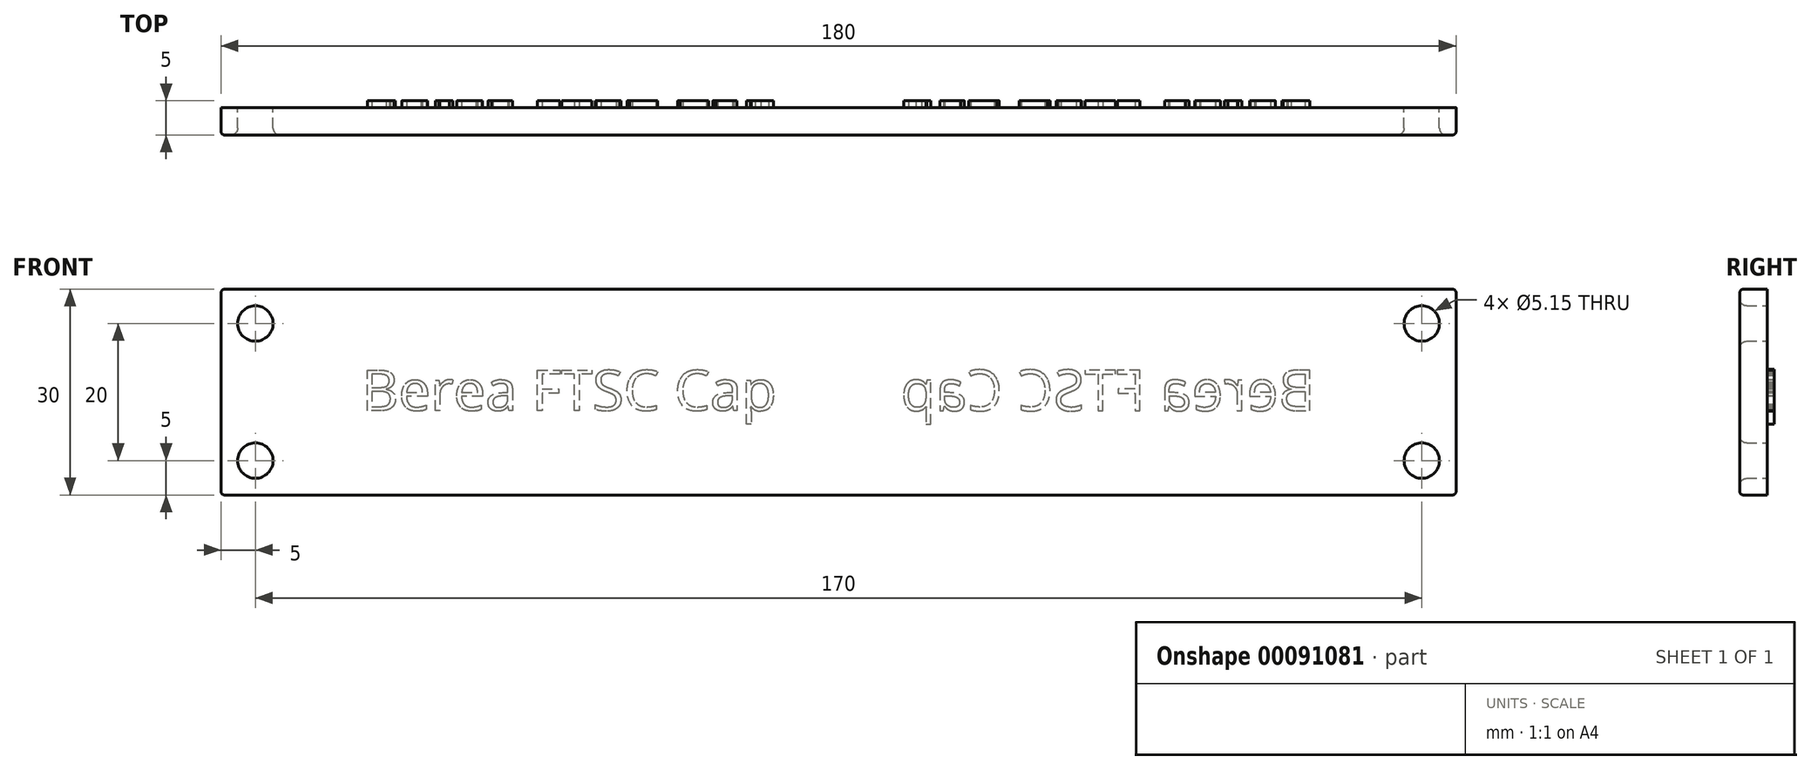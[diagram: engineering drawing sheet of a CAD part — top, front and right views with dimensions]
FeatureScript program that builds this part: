
annotation { "Feature Type Name" : "Feature", "Feature Type Description" : "" }
export const myFeature = defineFeature(function(context is Context, id is Id, definition is map)
    precondition{}
    {
        {
            var Q0;
            Q0=qCreatedBy(makeId("Front.planeOp"),FACE);
            var sketch = newSketch(context, id + "F0", { "sketchPlane" : qUnion([Q0])});
            skLineSegment(sketch, "E0.bottom", {"start": v(-90, -15) * mm, "end": v(90, -15) * mm});
            skLineSegment(sketch, "E0.top", {"start": v(-90, 15) * mm, "end": v(90, 15) * mm});
            skLineSegment(sketch, "E0.left", {"start": v(-90, -15) * mm, "end": v(-90, 15) * mm});
            skLineSegment(sketch, "E0.right", {"start": v(90, -15) * mm, "end": v(90, 15) * mm});
            skPoint(sketch, "E0.middle", {"position": v(0, 0) * mm});
            skCircle(sketch, "E1", {"center": v(-85, 10) * mm, "radius": 2.58 * mm});
            skPoint(sketch, "E2.start.orphan", {"position": v(-90, 0) * mm});
            skPoint(sketch, "E3.orphan", {"position": v(0, 15) * mm});
            skPoint(sketch, "E4.end.orphan", {"position": v(0, -15) * mm});
            skLineSegment(sketch, "E5", {"start": v(-90, 0) * mm, "end": v(0, 0) * mm, "construction": true});
            skLineSegment(sketch, "E6", {"start": v(0, 15) * mm, "end": v(0, -15) * mm, "construction": true});
            skCircle(sketch, "E7.MirrorC", {"center": v(-85, -10) * mm, "radius": 2.58 * mm});
            skCircle(sketch, "E8.MirrorC", {"center": v(85, 10) * mm, "radius": 2.58 * mm});
            skCircle(sketch, "E9.MirrorC", {"center": v(85, -10) * mm, "radius": 2.58 * mm});
            skSolve(sketch);
        }
        {
            var Q0;
            Q0=makeQuery(id+"F0.imprint","IMPRINT",FACE,{"disambiguationData":[TD([[makeQuery(id+"F0.imprint","IMPRINT",EDGE,{"derivedFrom":sQuery(id+"F0.wireOp",EDGE,"E0.bottom")}),1.0]])]});
            extrude(context, id + "F1", {"entities" : qUnion([Q0]), "depth" : 4 * mm});
        }
        {
            var Q0;
            Q0=makeQuery(id+"F1.opExtrude","CAP_EDGE",EDGE,{"disambiguationData":[OSD([sQuery(id+"F0.wireOp",EDGE,"E1")])],"isStart":false});
            var Q1;
            Q1=makeQuery(id+"F1.opExtrude","CAP_EDGE",EDGE,{"disambiguationData":[OSD([sQuery(id+"F0.wireOp",EDGE,"f5b72a5b-8583-449a-bdbf-9ac5a681e1fd0.MirrorC")])],"isStart":false});
            var Q2;
            Q2=makeQuery(id+"F1.opExtrude","CAP_EDGE",EDGE,{"disambiguationData":[OSD([sQuery(id+"F0.wireOp",EDGE,"2623e306-60f4-4522-aa65-1e3e8c2cf5b60.MirrorC")])],"isStart":false});
            var Q3;
            Q3=makeQuery(id+"F1.opExtrude","CAP_EDGE",EDGE,{"disambiguationData":[OSD([sQuery(id+"F0.wireOp",EDGE,"be81a34d-1d50-4ce7-a7a8-4484a1701fac0.MirrorC")])],"isStart":false});
            var Q4;
            Q4=makeQuery(id+"F1.opExtrude","CAP_EDGE",EDGE,{"disambiguationData":[OSD([sQuery(id+"F0.wireOp",EDGE,"E7.MirrorC")])],"isStart":false});
            var Q5;
            Q5=makeQuery(id+"F1.opExtrude","CAP_EDGE",EDGE,{"disambiguationData":[OSD([sQuery(id+"F0.wireOp",EDGE,"E8.MirrorC")])],"isStart":false});
            var Q6;
            Q6=makeQuery(id+"F1.opExtrude","CAP_EDGE",EDGE,{"disambiguationData":[OSD([sQuery(id+"F0.wireOp",EDGE,"E9.MirrorC")])],"isStart":false});
            fillet(context, id + "F2", {"entities" : qUnion([Q0, Q1, Q2, Q3, Q4, Q5, Q6]), "radius" : 1 * mm, "tangentPropagation" : true, "allowEdgeOverflow" : false});
        }
        {
            var Q0;
            Q0=makeQuery(id+"F1.opExtrude","CAP_EDGE",EDGE,{"disambiguationData":[OSD([sQuery(id+"F0.wireOp",EDGE,"E0.top")])],"isStart":false});
            var Q1;
            Q1=makeQuery(id+"F1.opExtrude","CAP_EDGE",EDGE,{"disambiguationData":[OSD([sQuery(id+"F0.wireOp",EDGE,"E0.left")])],"isStart":false});
            var Q2;
            Q2=makeQuery(id+"F1.opExtrude","CAP_EDGE",EDGE,{"disambiguationData":[OSD([sQuery(id+"F0.wireOp",EDGE,"E0.bottom")])],"isStart":false});
            var Q3;
            Q3=makeQuery(id+"F1.opExtrude","CAP_EDGE",EDGE,{"disambiguationData":[OSD([sQuery(id+"F0.wireOp",EDGE,"E0.right")])],"isStart":false});
            var Q4;
            Q4=makeQuery(id+"F1.opExtrude","SWEPT_EDGE",EDGE,{"disambiguationData":[OSD([sQuery(id+"F0.wireOp",EDGE,"E0.top"),sQuery(id+"F0.wireOp",EDGE,"E0.left")])]});
            var Q5;
            Q5=makeQuery(id+"F1.opExtrude","SWEPT_EDGE",EDGE,{"disambiguationData":[OSD([sQuery(id+"F0.wireOp",EDGE,"E0.bottom"),sQuery(id+"F0.wireOp",EDGE,"E0.left")])]});
            var Q6;
            Q6=makeQuery(id+"F1.opExtrude","SWEPT_EDGE",EDGE,{"disambiguationData":[OSD([sQuery(id+"F0.wireOp",EDGE,"E0.top"),sQuery(id+"F0.wireOp",EDGE,"E0.right")])]});
            var Q7;
            Q7=makeQuery(id+"F1.opExtrude","SWEPT_EDGE",EDGE,{"disambiguationData":[OSD([sQuery(id+"F0.wireOp",EDGE,"E0.bottom"),sQuery(id+"F0.wireOp",EDGE,"E0.right")])]});
            fillet(context, id + "F3", {"entities" : qUnion([Q0, Q1, Q2, Q3, Q4, Q5, Q6, Q7]), "radius" : .5 * mm, "tangentPropagation" : true, "allowEdgeOverflow" : false});
        }
        {
            var Q0;
            Q0=makeQuery(id+"F1.opExtrude","CAP_FACE",FACE,{"disambiguationData":[OSD([sQuery(id+"F0.wireOp",EDGE,"E0.bottom"),sQuery(id+"F0.wireOp",EDGE,"E0.top"),sQuery(id+"F0.wireOp",EDGE,"E0.left"),sQuery(id+"F0.wireOp",EDGE,"E0.right"),sQuery(id+"F0.wireOp",EDGE,"E1"),sQuery(id+"F0.wireOp",EDGE,"E7.MirrorC"),sQuery(id+"F0.wireOp",EDGE,"E8.MirrorC"),sQuery(id+"F0.wireOp",EDGE,"E9.MirrorC")])],"isStart":true});
            var sketch = newSketch(context, id + "F4", { "sketchPlane" : qUnion([Q0])});
            skText(sketch, "E10", { "text": "Berea FTSC Cap", "fontName": "OpenSans-Regular.ttf"});
            skLineSegment(sketch, "E11", {"start": v(0, 15) * mm, "end": v(0, -15) * mm, "construction": true});
            const initialGuessF4  = {"E10": [-0.0695, -0.0027, 1, 0, 0.00596]};
            skSetInitialGuess(sketch, initialGuessF4);
            skSolve(sketch);
        }
        {
            var Q0;
            Q0=qSketchRegion(id+"F4",true);
            extrude(context, id + "F5", {"entities" : qUnion([Q0]), "operationType" : NewBodyOperationType.ADD, "depth" : 1 * mm});
        }
        {
            var Q0;
            Q0=makeQuery(id+"F1.opExtrude","SWEPT_BODY",BODY,{"disambiguationData":[OSD([sQuery(id+"F0.wireOp",EDGE,"E0.bottom"),sQuery(id+"F0.wireOp",EDGE,"E0.top"),sQuery(id+"F0.wireOp",EDGE,"E0.left"),sQuery(id+"F0.wireOp",EDGE,"E0.right"),sQuery(id+"F0.wireOp",EDGE,"E1"),sQuery(id+"F0.wireOp",EDGE,"E7.MirrorC"),sQuery(id+"F0.wireOp",EDGE,"E8.MirrorC"),sQuery(id+"F0.wireOp",EDGE,"E9.MirrorC")])]});
            var Q1;
            Q1=makeQuery(id+"F5.opExtrude","SWEPT_FACE",FACE,{"disambiguationData":[OSD([sQuery(id+"F4.wireOp",EDGE,"E10.sketch_text.stroke-94")])]});
            var Q2;
            Q2=makeQuery(id+"F5.opExtrude","SWEPT_FACE",FACE,{"disambiguationData":[OSD([sQuery(id+"F4.wireOp",EDGE,"E10.sketch_text.stroke-169")])]});
            var Q3;
            Q3=makeQuery(id+"F5.opExtrude","SWEPT_FACE",FACE,{"disambiguationData":[OSD([sQuery(id+"F4.wireOp",EDGE,"E10.sketch_text.stroke-185")])]});
            var Q4;
            Q4=makeQuery(id+"F5.opExtrude","SWEPT_FACE",FACE,{"disambiguationData":[OSD([sQuery(id+"F4.wireOp",EDGE,"E10.sketch_text.stroke-125")])]});
            var Q5;
            Q5=makeQuery(id+"F5.opExtrude","SWEPT_FACE",FACE,{"disambiguationData":[OSD([sQuery(id+"F4.wireOp",EDGE,"E10.sketch_text.stroke-155")])]});
            var Q6;
            Q6=makeQuery(id+"F5.opExtrude","SWEPT_FACE",FACE,{"disambiguationData":[OSD([sQuery(id+"F4.wireOp",EDGE,"E10.sketch_text.stroke-65")])]});
            var Q7;
            Q7=makeQuery(id+"F5.opExtrude","SWEPT_FACE",FACE,{"disambiguationData":[OSD([sQuery(id+"F4.wireOp",EDGE,"E10.sketch_text.stroke-81")])]});
            var Q8;
            Q8=makeQuery(id+"F5.opExtrude","SWEPT_FACE",FACE,{"disambiguationData":[OSD([sQuery(id+"F4.wireOp",EDGE,"E10.sketch_text.stroke-67")])]});
            var Q9;
            Q9=makeQuery(id+"F5.opExtrude","SWEPT_FACE",FACE,{"disambiguationData":[OSD([sQuery(id+"F4.wireOp",EDGE,"E10.sketch_text.stroke-99")])]});
            var Q10;
            Q10=makeQuery(id+"F5.opExtrude","SWEPT_FACE",FACE,{"disambiguationData":[OSD([sQuery(id+"F4.wireOp",EDGE,"E10.sketch_text.stroke-127")])]});
            var Q11;
            Q11=makeQuery(id+"F5.opExtrude","SWEPT_FACE",FACE,{"disambiguationData":[OSD([sQuery(id+"F4.wireOp",EDGE,"E10.sketch_text.stroke-10")])]});
            var Q12;
            Q12=makeQuery(id+"F5.opExtrude","CAP_FACE",FACE,{"disambiguationData":[OSD([sQuery(id+"F4.wireOp",EDGE,"E10.sketch_text.stroke-9"),sQuery(id+"F4.wireOp",EDGE,"E10.sketch_text.stroke-10"),sQuery(id+"F4.wireOp",EDGE,"E10.sketch_text.stroke-11"),sQuery(id+"F4.wireOp",EDGE,"E10.sketch_text.stroke-12")])],"isStart":false});
            var Q13;
            Q13=makeQuery(id+"F5.opExtrude","SWEPT_FACE",FACE,{"disambiguationData":[OSD([sQuery(id+"F4.wireOp",EDGE,"E10.sketch_text.stroke-154")])]});
            var Q14;
            Q14=makeQuery(id+"F5.opExtrude","SWEPT_FACE",FACE,{"disambiguationData":[OSD([sQuery(id+"F4.wireOp",EDGE,"E10.sketch_text.stroke-1")])]});
            var Q15;
            Q15=makeQuery(id+"F5.opExtrude","CAP_FACE",FACE,{"disambiguationData":[OSD([sQuery(id+"F4.wireOp",EDGE,"E10.sketch_text.stroke-124"),sQuery(id+"F4.wireOp",EDGE,"E10.sketch_text.stroke-125"),sQuery(id+"F4.wireOp",EDGE,"E10.sketch_text.stroke-126"),sQuery(id+"F4.wireOp",EDGE,"E10.sketch_text.stroke-127"),sQuery(id+"F4.wireOp",EDGE,"E10.sketch_text.stroke-128"),sQuery(id+"F4.wireOp",EDGE,"E10.sketch_text.stroke-129"),sQuery(id+"F4.wireOp",EDGE,"E10.sketch_text.stroke-130"),sQuery(id+"F4.wireOp",EDGE,"E10.sketch_text.stroke-131"),sQuery(id+"F4.wireOp",EDGE,"E10.sketch_text.stroke-132"),sQuery(id+"F4.wireOp",EDGE,"E10.sketch_text.stroke-133"),sQuery(id+"F4.wireOp",EDGE,"E10.sketch_text.stroke-134"),sQuery(id+"F4.wireOp",EDGE,"E10.sketch_text.stroke-135"),sQuery(id+"F4.wireOp",EDGE,"E10.sketch_text.stroke-136"),sQuery(id+"F4.wireOp",EDGE,"E10.sketch_text.stroke-137"),sQuery(id+"F4.wireOp",EDGE,"E10.sketch_text.stroke-138")])],"isStart":false});
            var Q16;
            Q16=makeQuery(id+"F5.opExtrude","CAP_FACE",FACE,{"disambiguationData":[OSD([sQuery(id+"F4.wireOp",EDGE,"E10.sketch_text.stroke-34"),sQuery(id+"F4.wireOp",EDGE,"E10.sketch_text.stroke-35"),sQuery(id+"F4.wireOp",EDGE,"E10.sketch_text.stroke-36"),sQuery(id+"F4.wireOp",EDGE,"E10.sketch_text.stroke-37"),sQuery(id+"F4.wireOp",EDGE,"E10.sketch_text.stroke-38"),sQuery(id+"F4.wireOp",EDGE,"E10.sketch_text.stroke-39"),sQuery(id+"F4.wireOp",EDGE,"E10.sketch_text.stroke-40"),sQuery(id+"F4.wireOp",EDGE,"E10.sketch_text.stroke-41"),sQuery(id+"F4.wireOp",EDGE,"E10.sketch_text.stroke-42"),sQuery(id+"F4.wireOp",EDGE,"E10.sketch_text.stroke-43"),sQuery(id+"F4.wireOp",EDGE,"E10.sketch_text.stroke-44"),sQuery(id+"F4.wireOp",EDGE,"E10.sketch_text.stroke-45"),sQuery(id+"F4.wireOp",EDGE,"E10.sketch_text.stroke-46"),sQuery(id+"F4.wireOp",EDGE,"E10.sketch_text.stroke-47"),sQuery(id+"F4.wireOp",EDGE,"E10.sketch_text.stroke-48"),sQuery(id+"F4.wireOp",EDGE,"E10.sketch_text.stroke-49"),sQuery(id+"F4.wireOp",EDGE,"E10.sketch_text.stroke-50"),sQuery(id+"F4.wireOp",EDGE,"E10.sketch_text.stroke-51"),sQuery(id+"F4.wireOp",EDGE,"E10.sketch_text.stroke-52"),sQuery(id+"F4.wireOp",EDGE,"E10.sketch_text.stroke-53"),sQuery(id+"F4.wireOp",EDGE,"E10.sketch_text.stroke-54"),sQuery(id+"F4.wireOp",EDGE,"E10.sketch_text.stroke-55"),sQuery(id+"F4.wireOp",EDGE,"E10.sketch_text.stroke-56"),sQuery(id+"F4.wireOp",EDGE,"E10.sketch_text.stroke-57"),sQuery(id+"F4.wireOp",EDGE,"E10.sketch_text.stroke-58"),sQuery(id+"F4.wireOp",EDGE,"E10.sketch_text.stroke-59"),sQuery(id+"F4.wireOp",EDGE,"E10.sketch_text.stroke-60")])],"isStart":false});
            var Q17;
            Q17=makeQuery(id+"F5.opExtrude","SWEPT_FACE",FACE,{"disambiguationData":[OSD([sQuery(id+"F4.wireOp",EDGE,"E10.sketch_text.stroke-50")])]});
            var Q18;
            Q18=makeQuery(id+"F5.opExtrude","SWEPT_FACE",FACE,{"disambiguationData":[OSD([sQuery(id+"F4.wireOp",EDGE,"E10.sketch_text.stroke-2")])]});
            var Q19;
            Q19=makeQuery(id+"F5.opExtrude","SWEPT_FACE",FACE,{"disambiguationData":[OSD([sQuery(id+"F4.wireOp",EDGE,"E10.sketch_text.stroke-3")])]});
            var Q20;
            Q20=makeQuery(id+"F5.opExtrude","SWEPT_FACE",FACE,{"disambiguationData":[OSD([sQuery(id+"F4.wireOp",EDGE,"E10.sketch_text.stroke-5")])]});
            var Q21;
            Q21=makeQuery(id+"F5.opExtrude","SWEPT_FACE",FACE,{"disambiguationData":[OSD([sQuery(id+"F4.wireOp",EDGE,"E10.sketch_text.stroke-8")])]});
            var Q22;
            Q22=makeQuery(id+"F5.opExtrude","SWEPT_FACE",FACE,{"disambiguationData":[OSD([sQuery(id+"F4.wireOp",EDGE,"E10.sketch_text.stroke-98")])]});
            var Q23;
            Q23=makeQuery(id+"F5.opExtrude","SWEPT_FACE",FACE,{"disambiguationData":[OSD([sQuery(id+"F4.wireOp",EDGE,"E10.sketch_text.stroke-66")])]});
            var Q24;
            Q24=makeQuery(id+"F5.opExtrude","SWEPT_FACE",FACE,{"disambiguationData":[OSD([sQuery(id+"F4.wireOp",EDGE,"E10.sketch_text.stroke-153")])]});
            var Q25;
            Q25=makeQuery(id+"F5.opExtrude","SWEPT_FACE",FACE,{"disambiguationData":[OSD([sQuery(id+"F4.wireOp",EDGE,"E10.sketch_text.stroke-126")])]});
            var Q26;
            Q26=makeQuery(id+"F5.opExtrude","SWEPT_FACE",FACE,{"disambiguationData":[OSD([sQuery(id+"F4.wireOp",EDGE,"E10.sketch_text.stroke-183")])]});
            var Q27;
            Q27=makeQuery(id+"F5.opExtrude","SWEPT_FACE",FACE,{"disambiguationData":[OSD([sQuery(id+"F4.wireOp",EDGE,"E10.sketch_text.stroke-109")])]});
            var Q28;
            Q28=makeQuery(id+"F5.opExtrude","SWEPT_FACE",FACE,{"disambiguationData":[OSD([sQuery(id+"F4.wireOp",EDGE,"E10.sketch_text.stroke-186")])]});
            var Q29;
            Q29=makeQuery(id+"F5.opExtrude","SWEPT_FACE",FACE,{"disambiguationData":[OSD([sQuery(id+"F4.wireOp",EDGE,"E10.sketch_text.stroke-79")])]});
            var Q30;
            Q30=makeQuery(id+"F5.opExtrude","SWEPT_FACE",FACE,{"disambiguationData":[OSD([sQuery(id+"F4.wireOp",EDGE,"E10.sketch_text.stroke-110")])]});
            var Q31;
            Q31=makeQuery(id+"F5.opExtrude","SWEPT_FACE",FACE,{"disambiguationData":[OSD([sQuery(id+"F4.wireOp",EDGE,"E10.sketch_text.stroke-38")])]});
            var Q32;
            Q32=makeQuery(id+"F5.opExtrude","SWEPT_FACE",FACE,{"disambiguationData":[OSD([sQuery(id+"F4.wireOp",EDGE,"E10.sketch_text.stroke-24")])]});
            var Q33;
            Q33=makeQuery(id+"F5.opExtrude","SWEPT_FACE",FACE,{"disambiguationData":[OSD([sQuery(id+"F4.wireOp",EDGE,"E10.sketch_text.stroke-12")])]});
            var Q34;
            Q34=makeQuery(id+"F5.opExtrude","SWEPT_FACE",FACE,{"disambiguationData":[OSD([sQuery(id+"F4.wireOp",EDGE,"E10.sketch_text.stroke-100")])]});
            var Q35;
            Q35=makeQuery(id+"F5.opExtrude","SWEPT_FACE",FACE,{"disambiguationData":[OSD([sQuery(id+"F4.wireOp",EDGE,"E10.sketch_text.stroke-158")])]});
            var Q36;
            Q36=makeQuery(id+"F5.opExtrude","SWEPT_FACE",FACE,{"disambiguationData":[OSD([sQuery(id+"F4.wireOp",EDGE,"E10.sketch_text.stroke-142")])]});
            var Q37;
            Q37=makeQuery(id+"F5.opExtrude","SWEPT_FACE",FACE,{"disambiguationData":[OSD([sQuery(id+"F4.wireOp",EDGE,"E10.sketch_text.stroke-54")])]});
            var Q38;
            Q38=makeQuery(id+"F5.opExtrude","SWEPT_FACE",FACE,{"disambiguationData":[OSD([sQuery(id+"F4.wireOp",EDGE,"E10.sketch_text.stroke-25")])]});
            var Q39;
            Q39=makeQuery(id+"F5.opExtrude","SWEPT_FACE",FACE,{"disambiguationData":[OSD([sQuery(id+"F4.wireOp",EDGE,"E10.sketch_text.stroke-101")])]});
            var Q40;
            Q40=makeQuery(id+"F5.opExtrude","SWEPT_FACE",FACE,{"disambiguationData":[OSD([sQuery(id+"F4.wireOp",EDGE,"E10.sketch_text.stroke-69")])]});
            var Q41;
            Q41=makeQuery(id+"F5.opExtrude","SWEPT_FACE",FACE,{"disambiguationData":[OSD([sQuery(id+"F4.wireOp",EDGE,"E10.sketch_text.stroke-159")])]});
            var Q42;
            Q42=makeQuery(id+"F5.opExtrude","SWEPT_FACE",FACE,{"disambiguationData":[OSD([sQuery(id+"F4.wireOp",EDGE,"E10.sketch_text.stroke-85")])]});
            var Q43;
            Q43=makeQuery(id+"F5.opExtrude","SWEPT_FACE",FACE,{"disambiguationData":[OSD([sQuery(id+"F4.wireOp",EDGE,"E10.sketch_text.stroke-173")])]});
            var Q44;
            Q44=makeQuery(id+"F5.opExtrude","SWEPT_FACE",FACE,{"disambiguationData":[OSD([sQuery(id+"F4.wireOp",EDGE,"E10.sketch_text.stroke-40")])]});
            var Q45;
            Q45=makeQuery(id+"F5.opExtrude","SWEPT_FACE",FACE,{"disambiguationData":[OSD([sQuery(id+"F4.wireOp",EDGE,"E10.sketch_text.stroke-102")])]});
            var Q46;
            Q46=makeQuery(id+"F5.opExtrude","SWEPT_FACE",FACE,{"disambiguationData":[OSD([sQuery(id+"F4.wireOp",EDGE,"E10.sketch_text.stroke-86")])]});
            var Q47;
            Q47=makeQuery(id+"F5.opExtrude","SWEPT_FACE",FACE,{"disambiguationData":[OSD([sQuery(id+"F4.wireOp",EDGE,"E10.sketch_text.stroke-130")])]});
            var Q48;
            Q48=makeQuery(id+"F5.opExtrude","SWEPT_FACE",FACE,{"disambiguationData":[OSD([sQuery(id+"F4.wireOp",EDGE,"E10.sketch_text.stroke-103")])]});
            var Q49;
            Q49=makeQuery(id+"F5.opExtrude","SWEPT_FACE",FACE,{"disambiguationData":[OSD([sQuery(id+"F4.wireOp",EDGE,"E10.sketch_text.stroke-87")])]});
            var Q50;
            Q50=makeQuery(id+"F5.opExtrude","SWEPT_FACE",FACE,{"disambiguationData":[OSD([sQuery(id+"F4.wireOp",EDGE,"E10.sketch_text.stroke-145")])]});
            var Q51;
            Q51=makeQuery(id+"F5.opExtrude","SWEPT_FACE",FACE,{"disambiguationData":[OSD([sQuery(id+"F4.wireOp",EDGE,"E10.sketch_text.stroke-131")])]});
            var Q52;
            Q52=makeQuery(id+"F5.opExtrude","SWEPT_FACE",FACE,{"disambiguationData":[OSD([sQuery(id+"F4.wireOp",EDGE,"E10.sketch_text.stroke-28")])]});
            var Q53;
            Q53=makeQuery(id+"F5.opExtrude","SWEPT_FACE",FACE,{"disambiguationData":[OSD([sQuery(id+"F4.wireOp",EDGE,"E10.sketch_text.stroke-14")])]});
            var Q54;
            Q54=makeQuery(id+"F5.opExtrude","SWEPT_FACE",FACE,{"disambiguationData":[OSD([sQuery(id+"F4.wireOp",EDGE,"E10.sketch_text.stroke-88")])]});
            var Q55;
            Q55=makeQuery(id+"F5.opExtrude","SWEPT_FACE",FACE,{"disambiguationData":[OSD([sQuery(id+"F4.wireOp",EDGE,"E10.sketch_text.stroke-162")])]});
            var Q56;
            Q56=makeQuery(id+"F5.opExtrude","SWEPT_FACE",FACE,{"disambiguationData":[OSD([sQuery(id+"F4.wireOp",EDGE,"E10.sketch_text.stroke-176")])]});
            var Q57;
            Q57=makeQuery(id+"F5.opExtrude","SWEPT_FACE",FACE,{"disambiguationData":[OSD([sQuery(id+"F4.wireOp",EDGE,"E10.sketch_text.stroke-73")])]});
            var Q58;
            Q58=makeQuery(id+"F5.opExtrude","SWEPT_FACE",FACE,{"disambiguationData":[OSD([sQuery(id+"F4.wireOp",EDGE,"E10.sketch_text.stroke-59")])]});
            var Q59;
            Q59=makeQuery(id+"F5.opExtrude","SWEPT_FACE",FACE,{"disambiguationData":[OSD([sQuery(id+"F4.wireOp",EDGE,"E10.sketch_text.stroke-133")])]});
            var Q60;
            Q60=makeQuery(id+"F5.opExtrude","SWEPT_FACE",FACE,{"disambiguationData":[OSD([sQuery(id+"F4.wireOp",EDGE,"E10.sketch_text.stroke-119")])]});
            var Q61;
            Q61=makeQuery(id+"F5.opExtrude","SWEPT_FACE",FACE,{"disambiguationData":[OSD([sQuery(id+"F4.wireOp",EDGE,"E10.sketch_text.stroke-74")])]});
            var Q62;
            Q62=makeQuery(id+"F5.opExtrude","SWEPT_FACE",FACE,{"disambiguationData":[OSD([sQuery(id+"F4.wireOp",EDGE,"E10.sketch_text.stroke-44")])]});
            var Q63;
            Q63=makeQuery(id+"F5.opExtrude","SWEPT_FACE",FACE,{"disambiguationData":[OSD([sQuery(id+"F4.wireOp",EDGE,"E10.sketch_text.stroke-120")])]});
            var Q64;
            Q64=makeQuery(id+"F5.opExtrude","SWEPT_FACE",FACE,{"disambiguationData":[OSD([sQuery(id+"F4.wireOp",EDGE,"E10.sketch_text.stroke-90")])]});
            var Q65;
            Q65=makeQuery(id+"F5.opExtrude","SWEPT_FACE",FACE,{"disambiguationData":[OSD([sQuery(id+"F4.wireOp",EDGE,"E10.sketch_text.stroke-178")])]});
            var Q66;
            Q66=makeQuery(id+"F5.opExtrude","SWEPT_FACE",FACE,{"disambiguationData":[OSD([sQuery(id+"F4.wireOp",EDGE,"E10.sketch_text.stroke-45")])]});
            var Q67;
            Q67=makeQuery(id+"F5.opExtrude","SWEPT_FACE",FACE,{"disambiguationData":[OSD([sQuery(id+"F4.wireOp",EDGE,"E10.sketch_text.stroke-31")])]});
            var Q68;
            Q68=makeQuery(id+"F5.opExtrude","SWEPT_FACE",FACE,{"disambiguationData":[OSD([sQuery(id+"F4.wireOp",EDGE,"E10.sketch_text.stroke-135")])]});
            var Q69;
            Q69=makeQuery(id+"F5.opExtrude","SWEPT_FACE",FACE,{"disambiguationData":[OSD([sQuery(id+"F4.wireOp",EDGE,"E10.sketch_text.stroke-179")])]});
            var Q70;
            Q70=makeQuery(id+"F5.opExtrude","SWEPT_FACE",FACE,{"disambiguationData":[OSD([sQuery(id+"F4.wireOp",EDGE,"E10.sketch_text.stroke-165")])]});
            var Q71;
            Q71=makeQuery(id+"F5.opExtrude","SWEPT_FACE",FACE,{"disambiguationData":[OSD([sQuery(id+"F4.wireOp",EDGE,"E10.sketch_text.stroke-149")])]});
            var Q72;
            Q72=makeQuery(id+"F5.opExtrude","SWEPT_FACE",FACE,{"disambiguationData":[OSD([sQuery(id+"F4.wireOp",EDGE,"E10.sketch_text.stroke-136")])]});
            var Q73;
            Q73=makeQuery(id+"F5.opExtrude","SWEPT_FACE",FACE,{"disambiguationData":[OSD([sQuery(id+"F4.wireOp",EDGE,"E10.sketch_text.stroke-122")])]});
            var Q74;
            Q74=makeQuery(id+"F5.opExtrude","SWEPT_FACE",FACE,{"disambiguationData":[OSD([sQuery(id+"F4.wireOp",EDGE,"E10.sketch_text.stroke-106")])]});
            var Q75;
            Q75=makeQuery(id+"F5.opExtrude","SWEPT_FACE",FACE,{"disambiguationData":[OSD([sQuery(id+"F4.wireOp",EDGE,"E10.sketch_text.stroke-180")])]});
            var Q76;
            Q76=makeQuery(id+"F5.opExtrude","SWEPT_FACE",FACE,{"disambiguationData":[OSD([sQuery(id+"F4.wireOp",EDGE,"E10.sketch_text.stroke-166")])]});
            var Q77;
            Q77=makeQuery(id+"F5.opExtrude","SWEPT_FACE",FACE,{"disambiguationData":[OSD([sQuery(id+"F4.wireOp",EDGE,"E10.sketch_text.stroke-150")])]});
            var Q78;
            Q78=makeQuery(id+"F5.opExtrude","SWEPT_FACE",FACE,{"disambiguationData":[OSD([sQuery(id+"F4.wireOp",EDGE,"E10.sketch_text.stroke-76")])]});
            var Q79;
            Q79=makeQuery(id+"F5.opExtrude","SWEPT_FACE",FACE,{"disambiguationData":[OSD([sQuery(id+"F4.wireOp",EDGE,"E10.sketch_text.stroke-32")])]});
            var Q80;
            Q80=makeQuery(id+"F5.opExtrude","SWEPT_FACE",FACE,{"disambiguationData":[OSD([sQuery(id+"F4.wireOp",EDGE,"E10.sketch_text.stroke-181")])]});
            var Q81;
            Q81=makeQuery(id+"F5.opExtrude","SWEPT_FACE",FACE,{"disambiguationData":[OSD([sQuery(id+"F4.wireOp",EDGE,"E10.sketch_text.stroke-47")])]});
            var Q82;
            Q82=makeQuery(id+"F5.opExtrude","SWEPT_FACE",FACE,{"disambiguationData":[OSD([sQuery(id+"F4.wireOp",EDGE,"E10.sketch_text.stroke-123")])]});
            var Q83;
            Q83=makeQuery(id+"F5.opExtrude","SWEPT_FACE",FACE,{"disambiguationData":[OSD([sQuery(id+"F4.wireOp",EDGE,"E10.sketch_text.stroke-107")])]});
            var Q84;
            Q84=makeQuery(id+"F5.opExtrude","SWEPT_FACE",FACE,{"disambiguationData":[OSD([sQuery(id+"F4.wireOp",EDGE,"E10.sketch_text.stroke-48")])]});
            var Q85;
            Q85=makeQuery(id+"F5.opExtrude","SWEPT_FACE",FACE,{"disambiguationData":[OSD([sQuery(id+"F4.wireOp",EDGE,"E10.sketch_text.stroke-124")])]});
            var Q86;
            Q86=makeQuery(id+"F5.opExtrude","SWEPT_FACE",FACE,{"disambiguationData":[OSD([sQuery(id+"F4.wireOp",EDGE,"E10.sketch_text.stroke-108")])]});
            var Q87;
            Q87=makeQuery(id+"F5.opExtrude","CAP_FACE",FACE,{"disambiguationData":[OSD([sQuery(id+"F4.wireOp",EDGE,"E10.sketch_text.stroke-139"),sQuery(id+"F4.wireOp",EDGE,"E10.sketch_text.stroke-140"),sQuery(id+"F4.wireOp",EDGE,"E10.sketch_text.stroke-141"),sQuery(id+"F4.wireOp",EDGE,"E10.sketch_text.stroke-142"),sQuery(id+"F4.wireOp",EDGE,"E10.sketch_text.stroke-143"),sQuery(id+"F4.wireOp",EDGE,"E10.sketch_text.stroke-144"),sQuery(id+"F4.wireOp",EDGE,"E10.sketch_text.stroke-145"),sQuery(id+"F4.wireOp",EDGE,"E10.sketch_text.stroke-146"),sQuery(id+"F4.wireOp",EDGE,"E10.sketch_text.stroke-147"),sQuery(id+"F4.wireOp",EDGE,"E10.sketch_text.stroke-148"),sQuery(id+"F4.wireOp",EDGE,"E10.sketch_text.stroke-149"),sQuery(id+"F4.wireOp",EDGE,"E10.sketch_text.stroke-150"),sQuery(id+"F4.wireOp",EDGE,"E10.sketch_text.stroke-151"),sQuery(id+"F4.wireOp",EDGE,"E10.sketch_text.stroke-152"),sQuery(id+"F4.wireOp",EDGE,"E10.sketch_text.stroke-153"),sQuery(id+"F4.wireOp",EDGE,"E10.sketch_text.stroke-154"),sQuery(id+"F4.wireOp",EDGE,"E10.sketch_text.stroke-155"),sQuery(id+"F4.wireOp",EDGE,"E10.sketch_text.stroke-156"),sQuery(id+"F4.wireOp",EDGE,"E10.sketch_text.stroke-157"),sQuery(id+"F4.wireOp",EDGE,"E10.sketch_text.stroke-158"),sQuery(id+"F4.wireOp",EDGE,"E10.sketch_text.stroke-159"),sQuery(id+"F4.wireOp",EDGE,"E10.sketch_text.stroke-160"),sQuery(id+"F4.wireOp",EDGE,"E10.sketch_text.stroke-161"),sQuery(id+"F4.wireOp",EDGE,"E10.sketch_text.stroke-162"),sQuery(id+"F4.wireOp",EDGE,"E10.sketch_text.stroke-163"),sQuery(id+"F4.wireOp",EDGE,"E10.sketch_text.stroke-164"),sQuery(id+"F4.wireOp",EDGE,"E10.sketch_text.stroke-165")])],"isStart":false});
            var Q88;
            Q88=makeQuery(id+"F5.opExtrude","CAP_FACE",FACE,{"disambiguationData":[OSD([sQuery(id+"F4.wireOp",EDGE,"E10.sketch_text.stroke-21"),sQuery(id+"F4.wireOp",EDGE,"E10.sketch_text.stroke-22"),sQuery(id+"F4.wireOp",EDGE,"E10.sketch_text.stroke-23"),sQuery(id+"F4.wireOp",EDGE,"E10.sketch_text.stroke-24"),sQuery(id+"F4.wireOp",EDGE,"E10.sketch_text.stroke-25"),sQuery(id+"F4.wireOp",EDGE,"E10.sketch_text.stroke-26"),sQuery(id+"F4.wireOp",EDGE,"E10.sketch_text.stroke-27"),sQuery(id+"F4.wireOp",EDGE,"E10.sketch_text.stroke-28"),sQuery(id+"F4.wireOp",EDGE,"E10.sketch_text.stroke-29"),sQuery(id+"F4.wireOp",EDGE,"E10.sketch_text.stroke-30"),sQuery(id+"F4.wireOp",EDGE,"E10.sketch_text.stroke-31"),sQuery(id+"F4.wireOp",EDGE,"E10.sketch_text.stroke-32"),sQuery(id+"F4.wireOp",EDGE,"E10.sketch_text.stroke-33")])],"isStart":false});
            var Q89;
            Q89=makeQuery(id+"F5.opExtrude","SWEPT_FACE",FACE,{"disambiguationData":[OSD([sQuery(id+"F4.wireOp",EDGE,"E10.sketch_text.stroke-113")])]});
            var Q90;
            Q90=makeQuery(id+"F5.opExtrude","SWEPT_FACE",FACE,{"disambiguationData":[OSD([sQuery(id+"F4.wireOp",EDGE,"E10.sketch_text.stroke-37")])]});
            var Q91;
            Q91=makeQuery(id+"F5.opExtrude","SWEPT_FACE",FACE,{"disambiguationData":[OSD([sQuery(id+"F4.wireOp",EDGE,"E10.sketch_text.stroke-187")])]});
            var Q92;
            Q92=makeQuery(id+"F5.opExtrude","SWEPT_FACE",FACE,{"disambiguationData":[OSD([sQuery(id+"F4.wireOp",EDGE,"E10.sketch_text.stroke-0")])]});
            var Q93;
            Q93=makeQuery(id+"F5.opExtrude","SWEPT_FACE",FACE,{"disambiguationData":[OSD([sQuery(id+"F4.wireOp",EDGE,"E10.sketch_text.stroke-4")])]});
            var Q94;
            Q94=makeQuery(id+"F5.opExtrude","SWEPT_FACE",FACE,{"disambiguationData":[OSD([sQuery(id+"F4.wireOp",EDGE,"E10.sketch_text.stroke-82")])]});
            var Q95;
            Q95=makeQuery(id+"F5.opExtrude","SWEPT_FACE",FACE,{"disambiguationData":[OSD([sQuery(id+"F4.wireOp",EDGE,"E10.sketch_text.stroke-52")])]});
            var Q96;
            Q96=makeQuery(id+"F5.opExtrude","SWEPT_FACE",FACE,{"disambiguationData":[OSD([sQuery(id+"F4.wireOp",EDGE,"E10.sketch_text.stroke-49")])]});
            var Q97;
            Q97=makeQuery(id+"F5.opExtrude","SWEPT_FACE",FACE,{"disambiguationData":[OSD([sQuery(id+"F4.wireOp",EDGE,"E10.sketch_text.stroke-63")])]});
            var Q98;
            Q98=makeQuery(id+"F5.opExtrude","SWEPT_FACE",FACE,{"disambiguationData":[OSD([sQuery(id+"F4.wireOp",EDGE,"E10.sketch_text.stroke-21")])]});
            var Q99;
            Q99=makeQuery(id+"F5.opExtrude","SWEPT_FACE",FACE,{"disambiguationData":[OSD([sQuery(id+"F4.wireOp",EDGE,"E10.sketch_text.stroke-128")])]});
            var Q100;
            Q100=makeQuery(id+"F5.opExtrude","SWEPT_FACE",FACE,{"disambiguationData":[OSD([sQuery(id+"F4.wireOp",EDGE,"E10.sketch_text.stroke-55")])]});
            var Q101;
            Q101=makeQuery(id+"F5.opExtrude","SWEPT_FACE",FACE,{"disambiguationData":[OSD([sQuery(id+"F4.wireOp",EDGE,"E10.sketch_text.stroke-26")])]});
            var Q102;
            Q102=makeQuery(id+"F5.opExtrude","SWEPT_FACE",FACE,{"disambiguationData":[OSD([sQuery(id+"F4.wireOp",EDGE,"E10.sketch_text.stroke-174")])]});
            var Q103;
            Q103=makeQuery(id+"F5.opExtrude","SWEPT_FACE",FACE,{"disambiguationData":[OSD([sQuery(id+"F4.wireOp",EDGE,"E10.sketch_text.stroke-104")])]});
            var Q104;
            Q104=makeQuery(id+"F5.opExtrude","SWEPT_FACE",FACE,{"disambiguationData":[OSD([sQuery(id+"F4.wireOp",EDGE,"E10.sketch_text.stroke-72")])]});
            var Q105;
            Q105=makeQuery(id+"F5.opExtrude","SWEPT_FACE",FACE,{"disambiguationData":[OSD([sQuery(id+"F4.wireOp",EDGE,"E10.sketch_text.stroke-132")])]});
            var Q106;
            Q106=makeQuery(id+"F5.opExtrude","SWEPT_FACE",FACE,{"disambiguationData":[OSD([sQuery(id+"F4.wireOp",EDGE,"E10.sketch_text.stroke-43")])]});
            var Q107;
            Q107=makeQuery(id+"F5.opExtrude","SWEPT_FACE",FACE,{"disambiguationData":[OSD([sQuery(id+"F4.wireOp",EDGE,"E10.sketch_text.stroke-15")])]});
            var Q108;
            Q108=makeQuery(id+"F5.opExtrude","SWEPT_FACE",FACE,{"disambiguationData":[OSD([sQuery(id+"F4.wireOp",EDGE,"E10.sketch_text.stroke-89")])]});
            var Q109;
            Q109=makeQuery(id+"F5.opExtrude","SWEPT_FACE",FACE,{"disambiguationData":[OSD([sQuery(id+"F4.wireOp",EDGE,"E10.sketch_text.stroke-163")])]});
            var Q110;
            Q110=makeQuery(id+"F5.opExtrude","SWEPT_FACE",FACE,{"disambiguationData":[OSD([sQuery(id+"F4.wireOp",EDGE,"E10.sketch_text.stroke-30")])]});
            var Q111;
            Q111=makeQuery(id+"F5.opExtrude","SWEPT_FACE",FACE,{"disambiguationData":[OSD([sQuery(id+"F4.wireOp",EDGE,"E10.sketch_text.stroke-134")])]});
            var Q112;
            Q112=makeQuery(id+"F5.opExtrude","SWEPT_FACE",FACE,{"disambiguationData":[OSD([sQuery(id+"F4.wireOp",EDGE,"E10.sketch_text.stroke-121")])]});
            var Q113;
            Q113=makeQuery(id+"F5.opExtrude","CAP_FACE",FACE,{"disambiguationData":[OSD([sQuery(id+"F4.wireOp",EDGE,"E10.sketch_text.stroke-105"),sQuery(id+"F4.wireOp",EDGE,"E10.sketch_text.stroke-106"),sQuery(id+"F4.wireOp",EDGE,"E10.sketch_text.stroke-107"),sQuery(id+"F4.wireOp",EDGE,"E10.sketch_text.stroke-108"),sQuery(id+"F4.wireOp",EDGE,"E10.sketch_text.stroke-109"),sQuery(id+"F4.wireOp",EDGE,"E10.sketch_text.stroke-110"),sQuery(id+"F4.wireOp",EDGE,"E10.sketch_text.stroke-111"),sQuery(id+"F4.wireOp",EDGE,"E10.sketch_text.stroke-112"),sQuery(id+"F4.wireOp",EDGE,"E10.sketch_text.stroke-113"),sQuery(id+"F4.wireOp",EDGE,"E10.sketch_text.stroke-114"),sQuery(id+"F4.wireOp",EDGE,"E10.sketch_text.stroke-115"),sQuery(id+"F4.wireOp",EDGE,"E10.sketch_text.stroke-116"),sQuery(id+"F4.wireOp",EDGE,"E10.sketch_text.stroke-117"),sQuery(id+"F4.wireOp",EDGE,"E10.sketch_text.stroke-118"),sQuery(id+"F4.wireOp",EDGE,"E10.sketch_text.stroke-119"),sQuery(id+"F4.wireOp",EDGE,"E10.sketch_text.stroke-120"),sQuery(id+"F4.wireOp",EDGE,"E10.sketch_text.stroke-121"),sQuery(id+"F4.wireOp",EDGE,"E10.sketch_text.stroke-122"),sQuery(id+"F4.wireOp",EDGE,"E10.sketch_text.stroke-123")])],"isStart":false});
            var Q114;
            Q114=makeQuery(id+"F5.opExtrude","SWEPT_FACE",FACE,{"disambiguationData":[OSD([sQuery(id+"F4.wireOp",EDGE,"E10.sketch_text.stroke-92")])]});
            var Q115;
            Q115=makeQuery(id+"F5.opExtrude","SWEPT_FACE",FACE,{"disambiguationData":[OSD([sQuery(id+"F4.wireOp",EDGE,"E10.sketch_text.stroke-46")])]});
            var Q116;
            Q116=makeQuery(id+"F5.opExtrude","CAP_FACE",FACE,{"disambiguationData":[OSD([sQuery(id+"F4.wireOp",EDGE,"E10.sketch_text.stroke-61"),sQuery(id+"F4.wireOp",EDGE,"E10.sketch_text.stroke-62"),sQuery(id+"F4.wireOp",EDGE,"E10.sketch_text.stroke-63"),sQuery(id+"F4.wireOp",EDGE,"E10.sketch_text.stroke-64"),sQuery(id+"F4.wireOp",EDGE,"E10.sketch_text.stroke-65"),sQuery(id+"F4.wireOp",EDGE,"E10.sketch_text.stroke-66"),sQuery(id+"F4.wireOp",EDGE,"E10.sketch_text.stroke-67"),sQuery(id+"F4.wireOp",EDGE,"E10.sketch_text.stroke-68"),sQuery(id+"F4.wireOp",EDGE,"E10.sketch_text.stroke-69"),sQuery(id+"F4.wireOp",EDGE,"E10.sketch_text.stroke-70"),sQuery(id+"F4.wireOp",EDGE,"E10.sketch_text.stroke-71"),sQuery(id+"F4.wireOp",EDGE,"E10.sketch_text.stroke-72"),sQuery(id+"F4.wireOp",EDGE,"E10.sketch_text.stroke-73"),sQuery(id+"F4.wireOp",EDGE,"E10.sketch_text.stroke-74"),sQuery(id+"F4.wireOp",EDGE,"E10.sketch_text.stroke-75"),sQuery(id+"F4.wireOp",EDGE,"E10.sketch_text.stroke-76"),sQuery(id+"F4.wireOp",EDGE,"E10.sketch_text.stroke-77"),sQuery(id+"F4.wireOp",EDGE,"E10.sketch_text.stroke-78"),sQuery(id+"F4.wireOp",EDGE,"E10.sketch_text.stroke-79"),sQuery(id+"F4.wireOp",EDGE,"E10.sketch_text.stroke-80"),sQuery(id+"F4.wireOp",EDGE,"E10.sketch_text.stroke-81"),sQuery(id+"F4.wireOp",EDGE,"E10.sketch_text.stroke-82"),sQuery(id+"F4.wireOp",EDGE,"E10.sketch_text.stroke-83"),sQuery(id+"F4.wireOp",EDGE,"E10.sketch_text.stroke-84"),sQuery(id+"F4.wireOp",EDGE,"E10.sketch_text.stroke-85"),sQuery(id+"F4.wireOp",EDGE,"E10.sketch_text.stroke-86"),sQuery(id+"F4.wireOp",EDGE,"E10.sketch_text.stroke-87"),sQuery(id+"F4.wireOp",EDGE,"E10.sketch_text.stroke-88"),sQuery(id+"F4.wireOp",EDGE,"E10.sketch_text.stroke-89"),sQuery(id+"F4.wireOp",EDGE,"E10.sketch_text.stroke-90"),sQuery(id+"F4.wireOp",EDGE,"E10.sketch_text.stroke-91"),sQuery(id+"F4.wireOp",EDGE,"E10.sketch_text.stroke-92"),sQuery(id+"F4.wireOp",EDGE,"E10.sketch_text.stroke-93"),sQuery(id+"F4.wireOp",EDGE,"E10.sketch_text.stroke-94"),sQuery(id+"F4.wireOp",EDGE,"E10.sketch_text.stroke-95"),sQuery(id+"F4.wireOp",EDGE,"E10.sketch_text.stroke-96"),sQuery(id+"F4.wireOp",EDGE,"E10.sketch_text.stroke-97"),sQuery(id+"F4.wireOp",EDGE,"E10.sketch_text.stroke-98"),sQuery(id+"F4.wireOp",EDGE,"E10.sketch_text.stroke-99"),sQuery(id+"F4.wireOp",EDGE,"E10.sketch_text.stroke-100"),sQuery(id+"F4.wireOp",EDGE,"E10.sketch_text.stroke-101"),sQuery(id+"F4.wireOp",EDGE,"E10.sketch_text.stroke-102"),sQuery(id+"F4.wireOp",EDGE,"E10.sketch_text.stroke-103"),sQuery(id+"F4.wireOp",EDGE,"E10.sketch_text.stroke-104")])],"isStart":false});
            var Q117;
            Q117=makeQuery(id+"F5.opExtrude","SWEPT_FACE",FACE,{"disambiguationData":[OSD([sQuery(id+"F4.wireOp",EDGE,"E10.sketch_text.stroke-33")])]});
            var Q118;
            Q118=makeQuery(id+"F5.opExtrude","SWEPT_FACE",FACE,{"disambiguationData":[OSD([sQuery(id+"F4.wireOp",EDGE,"E10.sketch_text.stroke-93")])]});
            var Q119;
            Q119=makeQuery(id+"F5.opExtrude","SWEPT_FACE",FACE,{"disambiguationData":[OSD([sQuery(id+"F4.wireOp",EDGE,"E10.sketch_text.stroke-34")])]});
            var Q120;
            Q120=makeQuery(id+"F5.opExtrude","SWEPT_FACE",FACE,{"disambiguationData":[OSD([sQuery(id+"F4.wireOp",EDGE,"E10.sketch_text.stroke-152")])]});
            var Q121;
            Q121=makeQuery(id+"F5.opExtrude","SWEPT_FACE",FACE,{"disambiguationData":[OSD([sQuery(id+"F4.wireOp",EDGE,"E10.sketch_text.stroke-51")])]});
            var Q122;
            Q122=makeQuery(id+"F5.opExtrude","SWEPT_FACE",FACE,{"disambiguationData":[OSD([sQuery(id+"F4.wireOp",EDGE,"E10.sketch_text.stroke-6")])]});
            var Q123;
            Q123=makeQuery(id+"F5.opExtrude","SWEPT_FACE",FACE,{"disambiguationData":[OSD([sQuery(id+"F4.wireOp",EDGE,"E10.sketch_text.stroke-7")])]});
            var Q124;
            Q124=makeQuery(id+"F5.opExtrude","SWEPT_FACE",FACE,{"disambiguationData":[OSD([sQuery(id+"F4.wireOp",EDGE,"E10.sketch_text.stroke-156")])]});
            var Q125;
            Q125=makeQuery(id+"F5.opExtrude","SWEPT_FACE",FACE,{"disambiguationData":[OSD([sQuery(id+"F4.wireOp",EDGE,"E10.sketch_text.stroke-112")])]});
            var Q126;
            Q126=makeQuery(id+"F5.boolean.opBoolean","SPLIT",FACE,{"disambiguationData":[TD([makeQuery(id+"F5.opExtrude","SWEPT_FACE",FACE,{"disambiguationData":[OSD([sQuery(id+"F4.wireOp",EDGE,"E10.sketch_text.stroke-182")])]})])],"derivedFrom":makeQuery(id+"F1.opExtrude","CAP_FACE",FACE,{"disambiguationData":[OSD([sQuery(id+"F0.wireOp",EDGE,"E0.bottom"),sQuery(id+"F0.wireOp",EDGE,"E0.top"),sQuery(id+"F0.wireOp",EDGE,"E0.left"),sQuery(id+"F0.wireOp",EDGE,"E0.right"),sQuery(id+"F0.wireOp",EDGE,"E1"),sQuery(id+"F0.wireOp",EDGE,"E7.MirrorC"),sQuery(id+"F0.wireOp",EDGE,"E8.MirrorC"),sQuery(id+"F0.wireOp",EDGE,"E9.MirrorC")])],"isStart":true})});
            var Q127;
            Q127=makeQuery(id+"F5.opExtrude","SWEPT_FACE",FACE,{"disambiguationData":[OSD([sQuery(id+"F4.wireOp",EDGE,"E10.sketch_text.stroke-96")])]});
            var Q128;
            Q128=makeQuery(id+"F5.opExtrude","SWEPT_FACE",FACE,{"disambiguationData":[OSD([sQuery(id+"F4.wireOp",EDGE,"E10.sketch_text.stroke-114")])]});
            var Q129;
            Q129=makeQuery(id+"F5.opExtrude","SWEPT_FACE",FACE,{"disambiguationData":[OSD([sQuery(id+"F4.wireOp",EDGE,"E10.sketch_text.stroke-39")])]});
            var Q130;
            Q130=makeQuery(id+"F5.opExtrude","SWEPT_FACE",FACE,{"disambiguationData":[OSD([sQuery(id+"F4.wireOp",EDGE,"E10.sketch_text.stroke-13")])]});
            var Q131;
            Q131=makeQuery(id+"F5.opExtrude","SWEPT_FACE",FACE,{"disambiguationData":[OSD([sQuery(id+"F4.wireOp",EDGE,"E10.sketch_text.stroke-115")])]});
            var Q132;
            Q132=makeQuery(id+"F5.opExtrude","SWEPT_FACE",FACE,{"disambiguationData":[OSD([sQuery(id+"F4.wireOp",EDGE,"E10.sketch_text.stroke-56")])]});
            var Q133;
            Q133=makeQuery(id+"F5.opExtrude","SWEPT_FACE",FACE,{"disambiguationData":[OSD([sQuery(id+"F4.wireOp",EDGE,"E10.sketch_text.stroke-144")])]});
            var Q134;
            Q134=makeQuery(id+"F5.opExtrude","SWEPT_FACE",FACE,{"disambiguationData":[OSD([sQuery(id+"F4.wireOp",EDGE,"E10.sketch_text.stroke-190")])]});
            var Q135;
            Q135=makeQuery(id+"F5.opExtrude","SWEPT_FACE",FACE,{"disambiguationData":[OSD([sQuery(id+"F4.wireOp",EDGE,"E10.sketch_text.stroke-116")])]});
            var Q136;
            Q136=makeQuery(id+"F5.opExtrude","SWEPT_FACE",FACE,{"disambiguationData":[OSD([sQuery(id+"F4.wireOp",EDGE,"E10.sketch_text.stroke-41")])]});
            var Q137;
            Q137=makeQuery(id+"F5.opExtrude","SWEPT_FACE",FACE,{"disambiguationData":[OSD([sQuery(id+"F4.wireOp",EDGE,"E10.sketch_text.stroke-161")])]});
            var Q138;
            Q138=makeQuery(id+"F5.opExtrude","SWEPT_FACE",FACE,{"disambiguationData":[OSD([sQuery(id+"F4.wireOp",EDGE,"E10.sketch_text.stroke-146")])]});
            var Q139;
            Q139=makeQuery(id+"F5.opExtrude","SWEPT_FACE",FACE,{"disambiguationData":[OSD([sQuery(id+"F4.wireOp",EDGE,"E10.sketch_text.stroke-58")])]});
            var Q140;
            Q140=makeQuery(id+"F5.opExtrude","SWEPT_FACE",FACE,{"disambiguationData":[OSD([sQuery(id+"F4.wireOp",EDGE,"E10.sketch_text.stroke-105")])]});
            var Q141;
            Q141=makeQuery(id+"F5.opExtrude","SWEPT_FACE",FACE,{"disambiguationData":[OSD([sQuery(id+"F4.wireOp",EDGE,"E10.sketch_text.stroke-177")])]});
            var Q142;
            Q142=makeQuery(id+"F5.opExtrude","SWEPT_FACE",FACE,{"disambiguationData":[OSD([sQuery(id+"F4.wireOp",EDGE,"E10.sketch_text.stroke-77")])]});
            var Q143;
            Q143=makeQuery(id+"F5.opExtrude","SWEPT_FACE",FACE,{"disambiguationData":[OSD([sQuery(id+"F4.wireOp",EDGE,"E10.sketch_text.stroke-138")])]});
            var Q144;
            Q144=makeQuery(id+"F5.opExtrude","SWEPT_FACE",FACE,{"disambiguationData":[OSD([sQuery(id+"F4.wireOp",EDGE,"E10.sketch_text.stroke-111")])]});
            var Q145;
            Q145=makeQuery(id+"F5.opExtrude","SWEPT_FACE",FACE,{"disambiguationData":[OSD([sQuery(id+"F4.wireOp",EDGE,"E10.sketch_text.stroke-53")])]});
            var Q146;
            Q146=makeQuery(id+"F5.opExtrude","SWEPT_FACE",FACE,{"disambiguationData":[OSD([sQuery(id+"F4.wireOp",EDGE,"E10.sketch_text.stroke-141")])]});
            var Q147;
            Q147=makeQuery(id+"F5.opExtrude","SWEPT_FACE",FACE,{"disambiguationData":[OSD([sQuery(id+"F4.wireOp",EDGE,"E10.sketch_text.stroke-157")])]});
            var Q148;
            Q148=makeQuery(id+"F5.opExtrude","SWEPT_FACE",FACE,{"disambiguationData":[OSD([sQuery(id+"F4.wireOp",EDGE,"E10.sketch_text.stroke-64")])]});
            var Q149;
            Q149=makeQuery(id+"F5.boolean.opBoolean","SPLIT",FACE,{"disambiguationData":[TD([makeQuery(id+"F5.opExtrude","SWEPT_FACE",FACE,{"disambiguationData":[OSD([sQuery(id+"F4.wireOp",EDGE,"E10.sketch_text.stroke-53")])]})])],"derivedFrom":makeQuery(id+"F1.opExtrude","CAP_FACE",FACE,{"disambiguationData":[OSD([sQuery(id+"F0.wireOp",EDGE,"E0.bottom"),sQuery(id+"F0.wireOp",EDGE,"E0.top"),sQuery(id+"F0.wireOp",EDGE,"E0.left"),sQuery(id+"F0.wireOp",EDGE,"E0.right"),sQuery(id+"F0.wireOp",EDGE,"E1"),sQuery(id+"F0.wireOp",EDGE,"E7.MirrorC"),sQuery(id+"F0.wireOp",EDGE,"E8.MirrorC"),sQuery(id+"F0.wireOp",EDGE,"E9.MirrorC")])],"isStart":true})});
            var Q150;
            Q150=makeQuery(id+"F5.opExtrude","SWEPT_FACE",FACE,{"disambiguationData":[OSD([sQuery(id+"F4.wireOp",EDGE,"E10.sketch_text.stroke-36")])]});
            var Q151;
            Q151=makeQuery(id+"F5.opExtrude","SWEPT_FACE",FACE,{"disambiguationData":[OSD([sQuery(id+"F4.wireOp",EDGE,"E10.sketch_text.stroke-22")])]});
            var Q152;
            Q152=makeQuery(id+"F5.boolean.opBoolean","SPLIT",FACE,{"disambiguationData":[TD([makeQuery(id+"F5.opExtrude","SWEPT_FACE",FACE,{"disambiguationData":[OSD([sQuery(id+"F4.wireOp",EDGE,"E10.sketch_text.stroke-119")])]})])],"derivedFrom":makeQuery(id+"F1.opExtrude","CAP_FACE",FACE,{"disambiguationData":[OSD([sQuery(id+"F0.wireOp",EDGE,"E0.bottom"),sQuery(id+"F0.wireOp",EDGE,"E0.top"),sQuery(id+"F0.wireOp",EDGE,"E0.left"),sQuery(id+"F0.wireOp",EDGE,"E0.right"),sQuery(id+"F0.wireOp",EDGE,"E1"),sQuery(id+"F0.wireOp",EDGE,"E7.MirrorC"),sQuery(id+"F0.wireOp",EDGE,"E8.MirrorC"),sQuery(id+"F0.wireOp",EDGE,"E9.MirrorC")])],"isStart":true})});
            var Q153;
            Q153=makeQuery(id+"F5.boolean.opBoolean","SPLIT",FACE,{"disambiguationData":[TD([makeQuery(id+"F5.opExtrude","SWEPT_FACE",FACE,{"disambiguationData":[OSD([sQuery(id+"F4.wireOp",EDGE,"E10.sketch_text.stroke-158")])]})])],"derivedFrom":makeQuery(id+"F1.opExtrude","CAP_FACE",FACE,{"disambiguationData":[OSD([sQuery(id+"F0.wireOp",EDGE,"E0.bottom"),sQuery(id+"F0.wireOp",EDGE,"E0.top"),sQuery(id+"F0.wireOp",EDGE,"E0.left"),sQuery(id+"F0.wireOp",EDGE,"E0.right"),sQuery(id+"F0.wireOp",EDGE,"E1"),sQuery(id+"F0.wireOp",EDGE,"E7.MirrorC"),sQuery(id+"F0.wireOp",EDGE,"E8.MirrorC"),sQuery(id+"F0.wireOp",EDGE,"E9.MirrorC")])],"isStart":true})});
            var Q154;
            Q154=makeQuery(id+"F5.opExtrude","SWEPT_FACE",FACE,{"disambiguationData":[OSD([sQuery(id+"F4.wireOp",EDGE,"E10.sketch_text.stroke-9")])]});
            var Q155;
            Q155=makeQuery(id+"F5.opExtrude","SWEPT_FACE",FACE,{"disambiguationData":[OSD([sQuery(id+"F4.wireOp",EDGE,"E10.sketch_text.stroke-167")])]});
            var Q156;
            Q156=makeQuery(id+"F5.opExtrude","SWEPT_FACE",FACE,{"disambiguationData":[OSD([sQuery(id+"F4.wireOp",EDGE,"E10.sketch_text.stroke-95")])]});
            var Q157;
            Q157=makeQuery(id+"F5.opExtrude","SWEPT_FACE",FACE,{"disambiguationData":[OSD([sQuery(id+"F4.wireOp",EDGE,"E10.sketch_text.stroke-184")])]});
            var Q158;
            Q158=makeQuery(id+"F5.opExtrude","SWEPT_FACE",FACE,{"disambiguationData":[OSD([sQuery(id+"F4.wireOp",EDGE,"E10.sketch_text.stroke-84")])]});
            var Q159;
            Q159=makeQuery(id+"F5.opExtrude","SWEPT_FACE",FACE,{"disambiguationData":[OSD([sQuery(id+"F4.wireOp",EDGE,"E10.sketch_text.stroke-68")])]});
            var Q160;
            Q160=makeQuery(id+"F5.opExtrude","SWEPT_FACE",FACE,{"disambiguationData":[OSD([sQuery(id+"F4.wireOp",EDGE,"E10.sketch_text.stroke-143")])]});
            var Q161;
            Q161=makeQuery(id+"F5.opExtrude","SWEPT_FACE",FACE,{"disambiguationData":[OSD([sQuery(id+"F4.wireOp",EDGE,"E10.sketch_text.stroke-189")])]});
            var Q162;
            Q162=makeQuery(id+"F5.opExtrude","CAP_FACE",FACE,{"disambiguationData":[OSD([sQuery(id+"F4.wireOp",EDGE,"E10.sketch_text.stroke-13"),sQuery(id+"F4.wireOp",EDGE,"E10.sketch_text.stroke-14"),sQuery(id+"F4.wireOp",EDGE,"E10.sketch_text.stroke-15"),sQuery(id+"F4.wireOp",EDGE,"E10.sketch_text.stroke-16"),sQuery(id+"F4.wireOp",EDGE,"E10.sketch_text.stroke-17"),sQuery(id+"F4.wireOp",EDGE,"E10.sketch_text.stroke-18"),sQuery(id+"F4.wireOp",EDGE,"E10.sketch_text.stroke-19"),sQuery(id+"F4.wireOp",EDGE,"E10.sketch_text.stroke-20")])],"isStart":false});
            var Q163;
            Q163=makeQuery(id+"F5.opExtrude","SWEPT_FACE",FACE,{"disambiguationData":[OSD([sQuery(id+"F4.wireOp",EDGE,"E10.sketch_text.stroke-57")])]});
            var Q164;
            Q164=makeQuery(id+"F5.opExtrude","SWEPT_FACE",FACE,{"disambiguationData":[OSD([sQuery(id+"F4.wireOp",EDGE,"E10.sketch_text.stroke-29")])]});
            var Q165;
            Q165=makeQuery(id+"F5.opExtrude","SWEPT_FACE",FACE,{"disambiguationData":[OSD([sQuery(id+"F4.wireOp",EDGE,"E10.sketch_text.stroke-60")])]});
            var Q166;
            Q166=makeQuery(id+"F5.opExtrude","SWEPT_FACE",FACE,{"disambiguationData":[OSD([sQuery(id+"F4.wireOp",EDGE,"E10.sketch_text.stroke-148")])]});
            var Q167;
            Q167=makeQuery(id+"F5.opExtrude","SWEPT_FACE",FACE,{"disambiguationData":[OSD([sQuery(id+"F4.wireOp",EDGE,"E10.sketch_text.stroke-75")])]});
            var Q168;
            Q168=makeQuery(id+"F5.opExtrude","SWEPT_FACE",FACE,{"disambiguationData":[OSD([sQuery(id+"F4.wireOp",EDGE,"E10.sketch_text.stroke-91")])]});
            var Q169;
            Q169=makeQuery(id+"F5.opExtrude","SWEPT_FACE",FACE,{"disambiguationData":[OSD([sQuery(id+"F4.wireOp",EDGE,"E10.sketch_text.stroke-78")])]});
            var Q170;
            Q170=makeQuery(id+"F5.opExtrude","SWEPT_FACE",FACE,{"disambiguationData":[OSD([sQuery(id+"F4.wireOp",EDGE,"E10.sketch_text.stroke-62")])]});
            var Q171;
            Q171=makeQuery(id+"F5.opExtrude","SWEPT_FACE",FACE,{"disambiguationData":[OSD([sQuery(id+"F4.wireOp",EDGE,"E10.sketch_text.stroke-182")])]});
            var Q172;
            Q172=makeQuery(id+"F5.opExtrude","SWEPT_FACE",FACE,{"disambiguationData":[OSD([sQuery(id+"F4.wireOp",EDGE,"E10.sketch_text.stroke-11")])]});
            var Q173;
            Q173=makeQuery(id+"F5.opExtrude","SWEPT_FACE",FACE,{"disambiguationData":[OSD([sQuery(id+"F4.wireOp",EDGE,"E10.sketch_text.stroke-97")])]});
            var Q174;
            Q174=makeQuery(id+"F5.opExtrude","SWEPT_FACE",FACE,{"disambiguationData":[OSD([sQuery(id+"F4.wireOp",EDGE,"E10.sketch_text.stroke-23")])]});
            var Q175;
            Q175=makeQuery(id+"F5.opExtrude","SWEPT_FACE",FACE,{"disambiguationData":[OSD([sQuery(id+"F4.wireOp",EDGE,"E10.sketch_text.stroke-80")])]});
            var Q176;
            Q176=makeQuery(id+"F5.boolean.opBoolean","SPLIT",FACE,{"disambiguationData":[TD([makeQuery(id+"F5.opExtrude","SWEPT_FACE",FACE,{"disambiguationData":[OSD([sQuery(id+"F4.wireOp",EDGE,"E10.sketch_text.stroke-99")])]})])],"derivedFrom":makeQuery(id+"F1.opExtrude","CAP_FACE",FACE,{"disambiguationData":[OSD([sQuery(id+"F0.wireOp",EDGE,"E0.bottom"),sQuery(id+"F0.wireOp",EDGE,"E0.top"),sQuery(id+"F0.wireOp",EDGE,"E0.left"),sQuery(id+"F0.wireOp",EDGE,"E0.right"),sQuery(id+"F0.wireOp",EDGE,"E1"),sQuery(id+"F0.wireOp",EDGE,"E7.MirrorC"),sQuery(id+"F0.wireOp",EDGE,"E8.MirrorC"),sQuery(id+"F0.wireOp",EDGE,"E9.MirrorC")])],"isStart":true})});
            var Q177;
            Q177=makeQuery(id+"F5.opExtrude","SWEPT_FACE",FACE,{"disambiguationData":[OSD([sQuery(id+"F4.wireOp",EDGE,"E10.sketch_text.stroke-168")])]});
            var Q178;
            Q178=makeQuery(id+"F5.opExtrude","SWEPT_FACE",FACE,{"disambiguationData":[OSD([sQuery(id+"F4.wireOp",EDGE,"E10.sketch_text.stroke-188")])]});
            var Q179;
            Q179=makeQuery(id+"F5.opExtrude","SWEPT_FACE",FACE,{"disambiguationData":[OSD([sQuery(id+"F4.wireOp",EDGE,"E10.sketch_text.stroke-129")])]});
            var Q180;
            Q180=makeQuery(id+"F5.opExtrude","SWEPT_FACE",FACE,{"disambiguationData":[OSD([sQuery(id+"F4.wireOp",EDGE,"E10.sketch_text.stroke-27")])]});
            var Q181;
            Q181=makeQuery(id+"F5.opExtrude","SWEPT_FACE",FACE,{"disambiguationData":[OSD([sQuery(id+"F4.wireOp",EDGE,"E10.sketch_text.stroke-175")])]});
            var Q182;
            Q182=makeQuery(id+"F5.opExtrude","SWEPT_FACE",FACE,{"disambiguationData":[OSD([sQuery(id+"F4.wireOp",EDGE,"E10.sketch_text.stroke-42")])]});
            var Q183;
            Q183=makeQuery(id+"F5.opExtrude","SWEPT_FACE",FACE,{"disambiguationData":[OSD([sQuery(id+"F4.wireOp",EDGE,"E10.sketch_text.stroke-118")])]});
            var Q184;
            Q184=makeQuery(id+"F5.opExtrude","SWEPT_FACE",FACE,{"disambiguationData":[OSD([sQuery(id+"F4.wireOp",EDGE,"E10.sketch_text.stroke-151")])]});
            var Q185;
            Q185=makeQuery(id+"F5.opExtrude","SWEPT_FACE",FACE,{"disambiguationData":[OSD([sQuery(id+"F4.wireOp",EDGE,"E10.sketch_text.stroke-137")])]});
            var Q186;
            Q186=makeQuery(id+"F5.opExtrude","SWEPT_FACE",FACE,{"disambiguationData":[OSD([sQuery(id+"F4.wireOp",EDGE,"E10.sketch_text.stroke-83")])]});
            var Q187;
            Q187=makeQuery(id+"F5.boolean.opBoolean","SPLIT",FACE,{"disambiguationData":[TD([makeQuery(id+"F5.opExtrude","SWEPT_FACE",FACE,{"disambiguationData":[OSD([sQuery(id+"F4.wireOp",EDGE,"E10.sketch_text.stroke-90")])]})])],"derivedFrom":makeQuery(id+"F1.opExtrude","CAP_FACE",FACE,{"disambiguationData":[OSD([sQuery(id+"F0.wireOp",EDGE,"E0.bottom"),sQuery(id+"F0.wireOp",EDGE,"E0.top"),sQuery(id+"F0.wireOp",EDGE,"E0.left"),sQuery(id+"F0.wireOp",EDGE,"E0.right"),sQuery(id+"F0.wireOp",EDGE,"E1"),sQuery(id+"F0.wireOp",EDGE,"E7.MirrorC"),sQuery(id+"F0.wireOp",EDGE,"E8.MirrorC"),sQuery(id+"F0.wireOp",EDGE,"E9.MirrorC")])],"isStart":true})});
            var Q188;
            Q188=makeQuery(id+"F5.opExtrude","SWEPT_FACE",FACE,{"disambiguationData":[OSD([sQuery(id+"F4.wireOp",EDGE,"E10.sketch_text.stroke-139")])]});
            var Q189;
            Q189=makeQuery(id+"F5.opExtrude","SWEPT_FACE",FACE,{"disambiguationData":[OSD([sQuery(id+"F4.wireOp",EDGE,"E10.sketch_text.stroke-70")])]});
            var Q190;
            Q190=makeQuery(id+"F5.opExtrude","SWEPT_FACE",FACE,{"disambiguationData":[OSD([sQuery(id+"F4.wireOp",EDGE,"E10.sketch_text.stroke-160")])]});
            var Q191;
            Q191=makeQuery(id+"F5.opExtrude","SWEPT_FACE",FACE,{"disambiguationData":[OSD([sQuery(id+"F4.wireOp",EDGE,"E10.sketch_text.stroke-71")])]});
            var Q192;
            Q192=makeQuery(id+"F5.opExtrude","SWEPT_FACE",FACE,{"disambiguationData":[OSD([sQuery(id+"F4.wireOp",EDGE,"E10.sketch_text.stroke-117")])]});
            var Q193;
            Q193=makeQuery(id+"F5.opExtrude","SWEPT_FACE",FACE,{"disambiguationData":[OSD([sQuery(id+"F4.wireOp",EDGE,"E10.sketch_text.stroke-147")])]});
            var Q194;
            Q194=makeQuery(id+"F5.opExtrude","SWEPT_FACE",FACE,{"disambiguationData":[OSD([sQuery(id+"F4.wireOp",EDGE,"E10.sketch_text.stroke-164")])]});
            var Q195;
            Q195=makeQuery(id+"F5.opExtrude","SWEPT_FACE",FACE,{"disambiguationData":[OSD([sQuery(id+"F4.wireOp",EDGE,"E10.sketch_text.stroke-61")])]});
            var Q196;
            Q196=makeQuery(id+"F5.opExtrude","SWEPT_FACE",FACE,{"disambiguationData":[OSD([sQuery(id+"F4.wireOp",EDGE,"E10.sketch_text.stroke-19")])]});
            var Q197;
            Q197=makeQuery(id+"F5.opExtrude","SWEPT_FACE",FACE,{"disambiguationData":[OSD([sQuery(id+"F4.wireOp",EDGE,"E10.sketch_text.stroke-35")])]});
            var Q198;
            Q198=makeQuery(id+"F5.opExtrude","SWEPT_FACE",FACE,{"disambiguationData":[OSD([sQuery(id+"F4.wireOp",EDGE,"E10.sketch_text.stroke-140")])]});
            var Q199;
            Q199=makeQuery(id+"F5.opExtrude","SWEPT_FACE",FACE,{"disambiguationData":[OSD([sQuery(id+"F4.wireOp",EDGE,"E10.sketch_text.stroke-20")])]});
            var Q200;
            Q200=makeQuery(id+"F5.opExtrude","SWEPT_FACE",FACE,{"disambiguationData":[OSD([sQuery(id+"F4.wireOp",EDGE,"E10.sketch_text.stroke-16")])]});
            var Q201;
            Q201=makeQuery(id+"F5.opExtrude","SWEPT_FACE",FACE,{"disambiguationData":[OSD([sQuery(id+"F4.wireOp",EDGE,"E10.sketch_text.stroke-18")])]});
            var Q202;
            Q202=makeQuery(id+"F5.opExtrude","SWEPT_FACE",FACE,{"disambiguationData":[OSD([sQuery(id+"F4.wireOp",EDGE,"E10.sketch_text.stroke-17")])]});
            var Q203;
            Q203=qCreatedBy(makeId("Right.planeOp"),FACE);
            mirror(context, id + "F6", {"operationType" : NewBodyOperationType.ADD, "entities" : qUnion([Q0]), "faces" : qUnion([Q1, Q2, Q3, Q4, Q5, Q6, Q7, Q8, Q9, Q10, Q11, Q12, Q13, Q14, Q15, Q16, Q17, Q18, Q19, Q20, Q21, Q22, Q23, Q24, Q25, Q26, Q27, Q28, Q29, Q30, Q31, Q32, Q33, Q34, Q35, Q36, Q37, Q38, Q39, Q40, Q41, Q42, Q43, Q44, Q45, Q46, Q47, Q48, Q49, Q50, Q51, Q52, Q53, Q54, Q55, Q56, Q57, Q58, Q59, Q60, Q61, Q62, Q63, Q64, Q65, Q66, Q67, Q68, Q69, Q70, Q71, Q72, Q73, Q74, Q75, Q76, Q77, Q78, Q79, Q80, Q81, Q82, Q83, Q84, Q85, Q86, Q87, Q88, Q89, Q90, Q91, Q92, Q93, Q94, Q95, Q96, Q97, Q98, Q99, Q100, Q101, Q102, Q103, Q104, Q105, Q106, Q107, Q108, Q109, Q110, Q111, Q112, Q113, Q114, Q115, Q116, Q117, Q118, Q119, Q120, Q121, Q122, Q123, Q124, Q125, Q126, Q127, Q128, Q129, Q130, Q131, Q132, Q133, Q134, Q135, Q136, Q137, Q138, Q139, Q140, Q141, Q142, Q143, Q144, Q145, Q146, Q147, Q148, Q149, Q150, Q151, Q152, Q153, Q154, Q155, Q156, Q157, Q158, Q159, Q160, Q161, Q162, Q163, Q164, Q165, Q166, Q167, Q168, Q169, Q170, Q171, Q172, Q173, Q174, Q175, Q176, Q177, Q178, Q179, Q180, Q181, Q182, Q183, Q184, Q185, Q186, Q187, Q188, Q189, Q190, Q191, Q192, Q193, Q194, Q195, Q196, Q197, Q198, Q199, Q200, Q201, Q202]), "mirrorPlane" : qUnion([Q203])});
        }
    });
